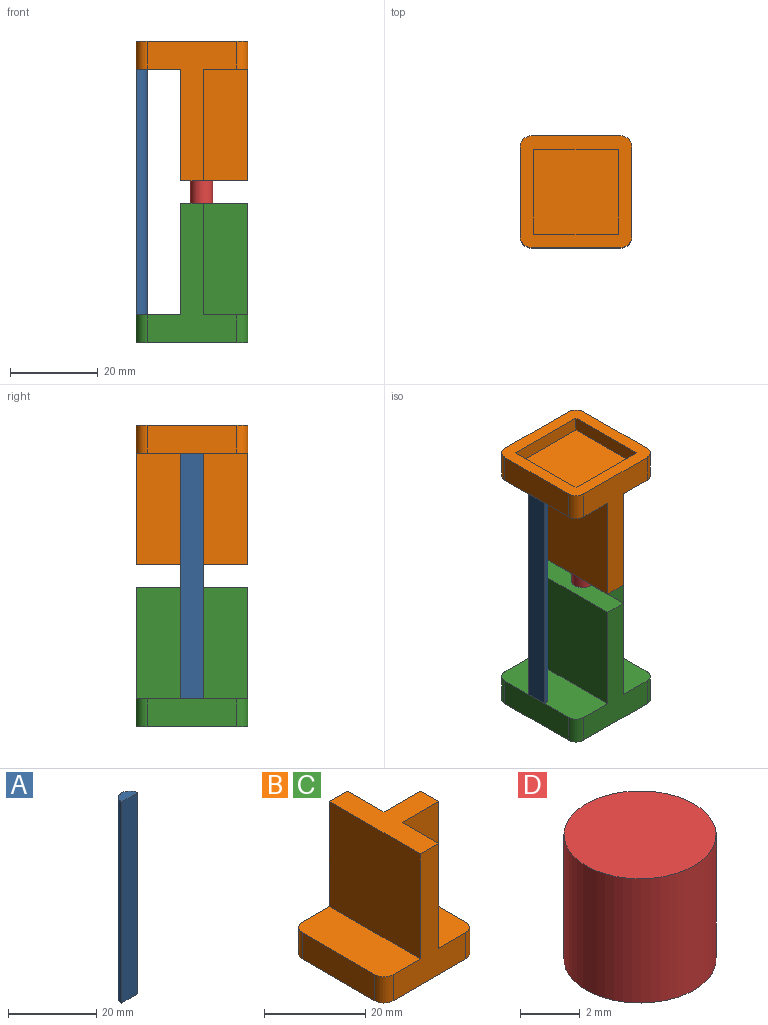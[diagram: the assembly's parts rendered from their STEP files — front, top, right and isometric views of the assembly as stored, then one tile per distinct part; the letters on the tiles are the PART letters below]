
ASSEMBLY  parts=4 mates=4
PART A: 4 faces, bbox 5.1x2.5x55.9 mm
  f0: plane 55.88x5.08mm, normal (0,-1,0), area 283.9mm2, adj f1,f2,f3
  f1: cylinder r=2.54mm len=55.88mm, axis (0,0,-1), area 445.9mm2, adj f0,f2,f3
  f2: plane 5.08x2.54mm, normal (0,0,1), area 10.1mm2, adj f0,f1
  f3: plane 5.08x2.54mm, normal (0,0,-1), area 10.1mm2, adj f0,f1
PART B: 23 faces, bbox 25.4x25.4x31.8 mm
  f0: plane 10.16x10.16mm, normal (0,0,1), area 101.8mm2, adj f2,f5,f11,f20,f21
  f1: plane 25.4x10.16mm, normal (0,0,1), area 255.3mm2, adj f3,f4,f5,f9,f10,f19
  f2: plane 31.75x20.32mm, normal (1,0,0), area 258.1mm2, adj f0,f6,f7,f8,f11,f17,f21,f22
  f3: plane 31.75x20.32mm, normal (0,1,0), area 258.1mm2, adj f1,f6,f7,f8,f9,f18,f19,f22
  f4: plane 20.32x6.35mm, normal (-1,0,0), area 129mm2, adj f1,f7,f9,f10
  f5: plane 31.75x20.32mm, normal (0,-1,0), area 258.1mm2, adj f0,f1,f7,f10,f11,f19,f20,f22
  f6: plane 10.16x10.16mm, normal (0,0,1), area 101.8mm2, adj f2,f3,f8,f17,f18
  f7: plane 25.4x25.4mm, normal (0,0,-1), area 267mm2, adj f2,f3,f4,f5,f8,f9,f10,f11
  f8: cylinder r=2.54mm len=6.35mm, axis (0,0,1), area 25.3mm2, adj f2,f3,f6,f7
  f9: cylinder r=2.54mm len=6.35mm, axis (0,0,-1), area 25.3mm2, adj f1,f3,f4,f7
  f10: cylinder r=2.54mm len=6.35mm, axis (0,0,1), area 25.3mm2, adj f1,f4,f5,f7
  f11: cylinder r=2.54mm len=6.35mm, axis (0,0,-1), area 25.3mm2, adj f0,f2,f5,f7
  f12: plane 19.3x3.3mm, normal (-1,0,0), area 63.7mm2, adj f7,f13,f15,f16
  f13: plane 19.3x3.3mm, normal (0,-1,0), area 63.7mm2, adj f7,f12,f14,f16
  f14: plane 19.3x3.3mm, normal (1,0,0), area 63.7mm2, adj f7,f13,f15,f16
  f15: plane 19.3x3.3mm, normal (0,1,0), area 63.7mm2, adj f7,f12,f14,f16
  f16: plane 19.3x19.3mm, normal (0,0,-1), area 372.6mm2, adj f12,f13,f14,f15
  f17: plane 25.4x10.16mm, normal (0,1,0), area 258.1mm2, adj f2,f6,f18,f22
  f18: plane 25.4x10.16mm, normal (1,0,0), area 258.1mm2, adj f3,f6,f17,f22
  f19: plane 25.4x25.4mm, normal (-1,0,0), area 645.2mm2, adj f1,f3,f5,f22
  f20: plane 25.4x10.16mm, normal (1,0,0), area 258.1mm2, adj f0,f5,f21,f22
  f21: plane 25.4x10.16mm, normal (0,-1,0), area 258.1mm2, adj f0,f2,f20,f22
  f22: plane 25.4x15.24mm, normal (0,0,1), area 180.6mm2, adj f2,f3,f5,f17,f18,f19,f20,f21
PART C: same geometry as B
PART D: 3 faces, bbox 5.1x5.1x5.1 mm
  f0: cylinder r=2.54mm len=5.08mm, axis (0,0,-1), area 81.1mm2, adj f1,f2
  f1: plane 5.08x5.08mm, normal (0,0,1), area 20.3mm2, adj f0
  f2: plane 5.08x5.08mm, normal (0,0,-1), area 20.3mm2, adj f0
PLACE A rot(axis=(0,0,-1),90deg) t=(22.86,-44.34,-20.43)mm
PLACE B rot(axis=(1,0,0),180deg) t=(-208.85,-33.97,41.8)mm
PLACE C t=(-208.85,42.23,-26.78)mm
PLACE D rot(axis=(1,0,0),180deg) t=(51.99,10.02,10.05)mm
MATE fastened D.f0 <-> B.f22  axis (0,0,1) through (21.93,4.13,10.05)mm
MATE fastened D.f0 <-> C.f22  axis (0,0,-1) through (21.93,4.13,4.97)mm
MATE planar A.f0 <-> C.f4  axis (-1,0,0) through (7.05,4.13,7.51)mm
MATE fastened A.f1 <-> C.f1  axis (0,0,-1) through (7.05,4.13,-20.43)mm
